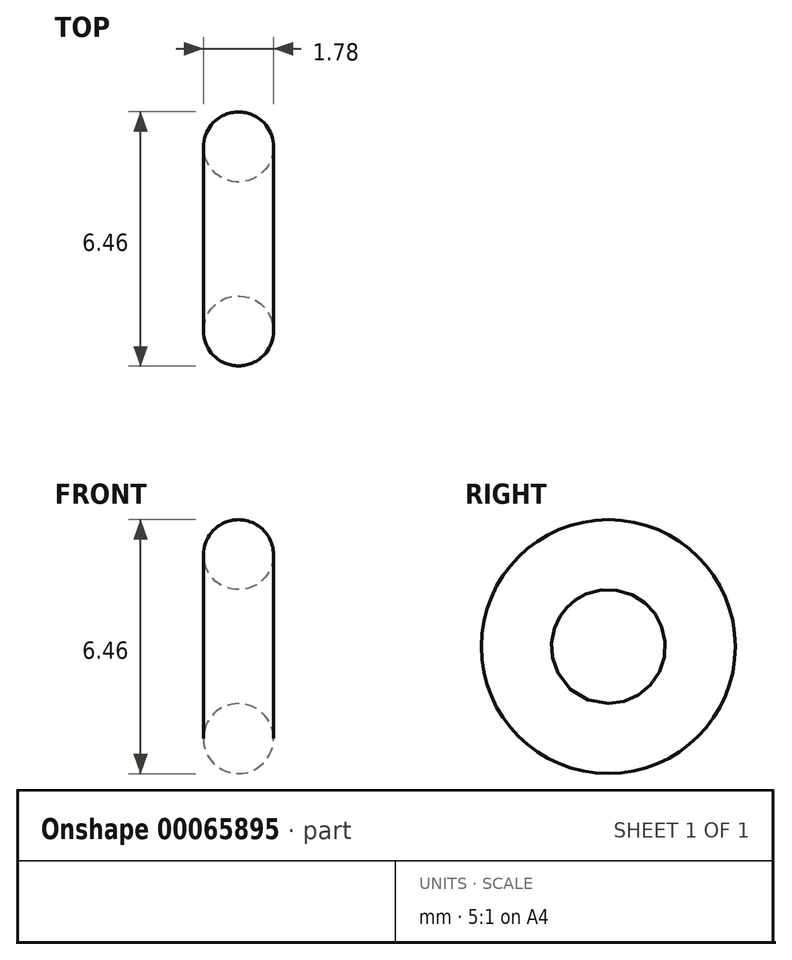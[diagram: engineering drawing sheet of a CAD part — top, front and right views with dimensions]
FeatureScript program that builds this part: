
annotation { "Feature Type Name" : "Feature", "Feature Type Description" : "" }
export const myFeature = defineFeature(function(context is Context, id is Id, definition is map)
    precondition{}
    {
        {
            var Q0;
            Q0=qCreatedBy(makeId("Front.planeOp"),FACE);
            var sketch = newSketch(context, id + "F0", { "sketchPlane" : qUnion([Q0])});
            skLineSegment(sketch, "E0", {"start": v(0, 0) * mm, "end": v(-6.06, 0) * mm, "construction": true});
            skCircle(sketch, "E1", {"center": v(0, 2.34) * mm, "radius": 0.89 * mm});
            skSolve(sketch);
        }
        {
            var Q0;
            Q0=makeQuery(id+"F0.imprint","IMPRINT",FACE,{"disambiguationData":[TD([[makeQuery(id+"F0.imprint","IMPRINT",EDGE,{"derivedFrom":sQuery(id+"F0.wireOp",EDGE,"E1")}),1.0]])]});
            var Q1;
            Q1=sQuery(id+"F0.wireOp",EDGE,"E0");
            revolve(context, id + "F1", {"entities" : qUnion([Q0]), "axis" : qUnion([Q1]), "revolveType" : RevolveType.FULL});
        }
    });
